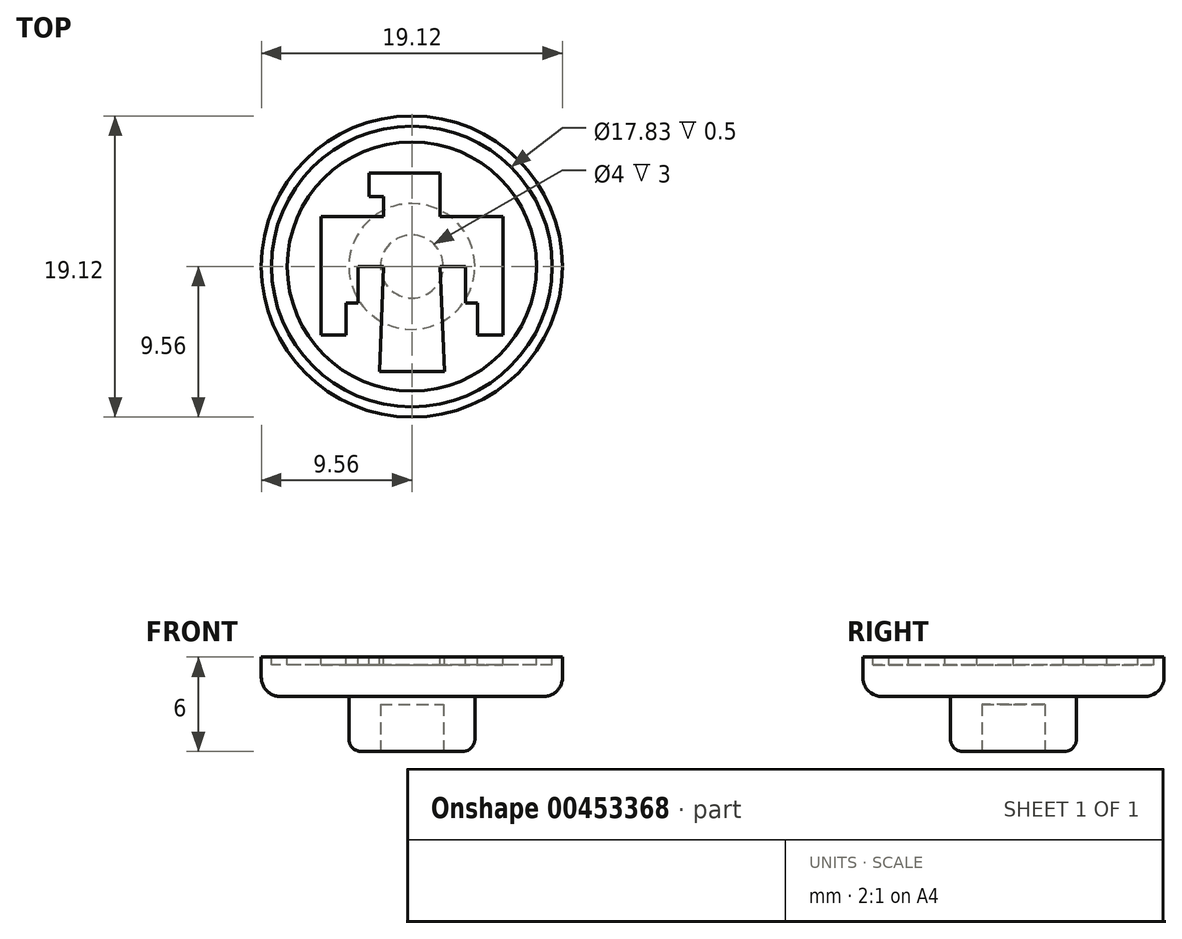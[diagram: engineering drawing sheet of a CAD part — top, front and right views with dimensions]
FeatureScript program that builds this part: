
annotation { "Feature Type Name" : "Feature", "Feature Type Description" : "" }
export const myFeature = defineFeature(function(context is Context, id is Id, definition is map)
    precondition{}
    {
        {
            var Q0;
            Q0=qCreatedBy(makeId("Top.planeOp"),FACE);
            var sketch = newSketch(context, id + "F0", { "sketchPlane" : qUnion([Q0])});
            skCircle(sketch, "E0", {"center": v(0, 0) * mm, "radius": 9.56 * mm});
            skSolve(sketch);
        }
        {
            var Q0;
            Q0=makeQuery(id+"F0.imprint","IMPRINT",FACE,{"disambiguationData":[TD([[makeQuery(id+"F0.imprint","IMPRINT",EDGE,{"derivedFrom":sQuery(id+"F0.wireOp",EDGE,"E0")}),1.0]])]});
            extrude(context, id + "F1", {"entities" : qUnion([Q0]), "depth" : 2.5 * mm, "offsetDistance" : 25 * mm});
        }
        {
            var Q0;
            Q0=makeQuery(id+"F1.opExtrude","CAP_FACE",FACE,{"disambiguationData":[OSD([sQuery(id+"F0.wireOp",EDGE,"E0")])],"isStart":false});
            var sketch = newSketch(context, id + "F2", { "sketchPlane" : qUnion([Q0])});
            skLineSegment(sketch, "E1", {"start": v(-2.7, 5.93) * mm, "end": v(1.8, 5.93) * mm});
            skLineSegment(sketch, "E2", {"start": v(1.8, 5.93) * mm, "end": v(1.8, 3.18) * mm});
            skLineSegment(sketch, "E3", {"start": v(1.8, 3.18) * mm, "end": v(5.78, 3.18) * mm});
            skLineSegment(sketch, "E4", {"start": v(5.78, 3.18) * mm, "end": v(5.78, -4.35) * mm});
            skLineSegment(sketch, "E5", {"start": v(5.78, -4.35) * mm, "end": v(4.17, -4.35) * mm});
            skLineSegment(sketch, "E6", {"start": v(4.17, -4.35) * mm, "end": v(4.17, -2.32) * mm});
            skLineSegment(sketch, "E7", {"start": v(4.17, -2.32) * mm, "end": v(3.41, -2.32) * mm});
            skLineSegment(sketch, "E8", {"start": v(3.41, -2.32) * mm, "end": v(3.41, 0) * mm});
            skLineSegment(sketch, "E9", {"start": v(3.41, 0) * mm, "end": v(1.8, 0) * mm});
            skLineSegment(sketch, "E10", {"start": v(2.06, -6.66) * mm, "end": v(0, -6.66) * mm});
            skLineSegment(sketch, "E11", {"start": v(-2.7, 5.93) * mm, "end": v(-2.7, 4.43) * mm});
            skLineSegment(sketch, "E12", {"start": v(-2.7, 4.43) * mm, "end": v(-1.8, 4.43) * mm});
            skLineSegment(sketch, "E13.MirrorCS", {"start": v(-1.8, 3.18) * mm, "end": v(-5.78, 3.18) * mm});
            skLineSegment(sketch, "E14.MirrorCS", {"start": v(-5.78, 3.18) * mm, "end": v(-5.78, -4.35) * mm});
            skLineSegment(sketch, "E15.MirrorCS", {"start": v(-4.17, -4.35) * mm, "end": v(-4.17, -2.32) * mm});
            skLineSegment(sketch, "E16.MirrorCS", {"start": v(-4.17, -2.32) * mm, "end": v(-3.41, -2.32) * mm});
            skLineSegment(sketch, "E17.MirrorCS", {"start": v(-3.41, -2.32) * mm, "end": v(-3.41, 0) * mm});
            skLineSegment(sketch, "E18.MirrorCS", {"start": v(-3.41, 0) * mm, "end": v(-1.8, 0) * mm});
            skLineSegment(sketch, "E19.MirrorCS", {"start": v(-5.78, -4.35) * mm, "end": v(-4.17, -4.35) * mm});
            skLineSegment(sketch, "E20.MirrorCS", {"start": v(-2.06, -6.66) * mm, "end": v(0, -6.66) * mm});
            skLineSegment(sketch, "E21", {"start": v(-1.8, 4.43) * mm, "end": v(-1.8, 3.18) * mm});
            skCircle(sketch, "E22", {"center": v(0, 0) * mm, "radius": 7.92 * mm});
            skCircle(sketch, "E23", {"center": v(0, 0) * mm, "radius": 8.92 * mm});
            skLineSegment(sketch, "E24", {"start": v(-2.06, -6.66) * mm, "end": v(-1.8, 0) * mm});
            skLineSegment(sketch, "E25", {"start": v(2.06, -6.66) * mm, "end": v(1.8, 0) * mm});
            skSolve(sketch);
        }
        {
            var Q0;
            Q0=makeQuery(id+"F2.imprint","IMPRINT",FACE,{"disambiguationData":[TD([[makeQuery(id+"F2.imprint","IMPRINT",EDGE,{"derivedFrom":sQuery(id+"F2.wireOp",EDGE,"E1")}),-1.0]])]});
            var Q1;
            Q1=makeQuery(id+"F2.imprint","IMPRINT",FACE,{"disambiguationData":[TD([[makeQuery(id+"F2.imprint","IMPRINT",EDGE,{"derivedFrom":sQuery(id+"F2.wireOp",EDGE,"E22")}),-1.0]])]});
            extrude(context, id + "F3", {"entities" : qUnion([Q0, Q1]), "operationType" : NewBodyOperationType.REMOVE, "oppositeDirection" : true, "depth" : .5 * mm, "offsetDistance" : 25 * mm});
        }
        {
            var Q0;
            Q0=makeQuery(id+"F1.opExtrude","CAP_FACE",FACE,{"disambiguationData":[OSD([sQuery(id+"F0.wireOp",EDGE,"E0")])],"isStart":true});
            var sketch = newSketch(context, id + "F4", { "sketchPlane" : qUnion([Q0])});
            skCircle(sketch, "E26", {"center": v(0, 0) * mm, "radius": 4 * mm});
            skSolve(sketch);
        }
        {
            var Q0;
            Q0=makeQuery(id+"F4.imprint","IMPRINT",FACE,{"disambiguationData":[TD([[makeQuery(id+"F4.imprint","IMPRINT",EDGE,{"derivedFrom":sQuery(id+"F4.wireOp",EDGE,"E26")}),1.0]])]});
            extrude(context, id + "F5", {"entities" : qUnion([Q0]), "operationType" : NewBodyOperationType.ADD, "depth" : 3.5 * mm, "offsetDistance" : 25 * mm});
        }
        {
            var Q0;
            Q0=makeQuery(id+"F1.opExtrude","CAP_EDGE",EDGE,{"disambiguationData":[OSD([sQuery(id+"F0.wireOp",EDGE,"E0")])],"isStart":true});
            fillet(context, id + "F6", {"entities" : qUnion([Q0]), "radius" : 1.2 * mm, "tangentPropagation" : true, "allowEdgeOverflow" : false});
        }
        {
            var Q0;
            Q0=makeQuery(id+"F5.opExtrude","CAP_FACE",FACE,{"disambiguationData":[OSD([sQuery(id+"F4.wireOp",EDGE,"E26")])],"isStart":false});
            var sketch = newSketch(context, id + "F7", { "sketchPlane" : qUnion([Q0])});
            skCircle(sketch, "E27", {"center": v(0, 0) * mm, "radius": 2 * mm});
            skSolve(sketch);
        }
        {
            var Q0;
            Q0=makeQuery(id+"F7.imprint","IMPRINT",FACE,{"disambiguationData":[TD([[makeQuery(id+"F7.imprint","IMPRINT",EDGE,{"derivedFrom":sQuery(id+"F7.wireOp",EDGE,"E27")}),1.0]])]});
            extrude(context, id + "F8", {"entities" : qUnion([Q0]), "operationType" : NewBodyOperationType.REMOVE, "oppositeDirection" : true, "depth" : 3 * mm, "offsetDistance" : 25 * mm});
        }
        {
            var Q0;
            Q0=makeQuery(id+"F5.opExtrude","CAP_EDGE",EDGE,{"disambiguationData":[OSD([sQuery(id+"F4.wireOp",EDGE,"E26")])],"isStart":false});
            fillet(context, id + "F9", {"entities" : qUnion([Q0]), "radius" : 0.8 * mm, "tangentPropagation" : true, "allowEdgeOverflow" : false});
        }
    });
